# Revit family: V801
name_source: partatom
category: Specialty Equipment
revit_build: Autodesk Revit Architecture 2012 (Build: 20110309_2315(x64)
units: mm (PartAtom-declared; Revit-internal decimal feet)

## types (1)
- V801
    Additional Features = See brochure
    Back Circuit Panel Height = 21.05 "
    Back Circuit Panel Height from Bottom = 11.65 "
    Back Circuit Panel Width = 35.41 "
    Connectivity- Digital Tuner = V801-AVT
    Connectivity- Input Terminals. Analog = VGA 15-pin D-sub, 5 BNC (RGBHV, DVD/HD, S-Video or Video), BNC Composite
    Connectivity- Input Terminals. Audio = Stereo Mini-Jack, HDMI Audio, DisplayPort Audio
    Connectivity- Input Terminals. Digital = Display Port, HDMI, DVI-D
    Connectivity- Input Terminals. External Control = RS-232C, Ethernet (RJ45), IR Remote, DDC/CI
    Connectivity- Output Terminals. Audio = Stereo Mini-Jack, External Speaker Jack (2)
    Connectivity- Output Terminals. Digital = DVI-D
    Connectivity- Output Terminals. External Control = RS-232C
    Connectivity- PC/Mac Signal Compatibility = Yes
    Connectivity- Speakers = Integrated (10W x 2)
    Environmental Conditions- Operating Altitude = 9843ft / 3000m
    Environmental Conditions- Operating Humidity = 20-80%
    Environmental Conditions- Operating Temperature = 41-104 degF / 5-40 degC
    Height from Floor = 26 "
    LCD- Active Screen Area (W x H) = 69.7 x 39.2 in. / 1771.2 x 996.3 mm
    LCD- Aspect Ratio = 16 : 9
    LCD- Brightness (Typical/Max) = 320 cd/m2 / 460 cd/m2
    LCD- Contrast Ratio (Typical) = 5000 : 1
    LCD- Displayable Colors = More than 1 billion
    LCD- Native Resolution = 1920 x 1080
    LCD- Orientation = Landscape / Portrait
    LCD- Panel Technology = UV2 A
    LCD- Viewable Image Size = 80"
    LCD- Viewing Angle = 178deg Vert., 178deg Hor. (89U/89D/89L/89R) at CR>10
    Limited Warranty = 3 years parts and labor, including backlight
    Manufacturer = NEC Display
    Optional Accessories = See brochure
    Panel Height = 41.78 "
    Panel Thickness = 1.68 "
    Panel Thickness Overall = 3.42 "
    Panel Width = 1.17 "
    Panel Width Overall = 72.29 "
    Physical Specs- Bezel Width (L/R, T/B) = 1.2in/1.2in, 1.2in/1.2in;  29.7mm/29.7mm, 29.7mm/29.7mm
    Physical Specs- Net Dimensions (w/o stand- WxHxD) = 72.3 x 41.8x 3.4in / 1836.2 x 1061.3 x 86.9mm
    Physical Specs- Net Weight (w/o stand) = 132.3 lbs / 60 kgs
    Physical Specs- VESA Hole Configuration = 400 x 400mm (4-hole)
    Power Consumption- ECO Mode Standby = <2W
    Power Consumption- On (Typical) = 230W
    Ships with = See brochure
    URL = necdisplay.com
    c1 = 2.5 "
    c2 = 0.08 "

## geometry (parser evidence)
native form markers: Sweep x20
no freeform markers — native parametric forms only
